# Revit family: IS_Ceralook_BC176_BIM_GB
name_source: partatom
category: Plumbing Fixtures
revit_build: Autodesk Revit 2017 (Build: 20160225_1515(x64)
units: mm (PartAtom-declared; Revit-internal decimal feet)

## family parameters
Always vertical = No
Cut with Voids When Loaded = No
OmniClass Number = 23.45.55.17
OmniClass Title = Mixing Faucets
Part Type = Normal
Room Calculation Point = No
Round Connector Dimension = Use Diameter
Shared = No
Work Plane-Based = No

## types (1)
- BC176AA - CLOOK SNK MXR SDE/HDL P/O HS/1F BLUE ST
    Accessories = www.idealspec.co.uk
    AreaUnits = millimeters
    AssetType = Fixed
    BIMObjectName = IS_IdealStandard_SinkMixer_Ceralook_BC176
    Brand = IdealStandard
    Category = Plumbing
    CisternCapacity = 0 m³
    Color = Chrome
    ConnectionType = Plumbing
    Description = BC176 CLOOK SNK MXR SDE/HDL P/O HS/1F BLUE ST
    DurationUnit = year
    ExpectedLife = 5
    Features = BC176 Sink Mixer Ceralook kitchen mixer with high spout L and handshower with BlueStart Technology
    Finish = Chrome
    FlushRate = 0 m³
    FlushingRate = 0
    HasGrabHandles = No
    HasIntegralShutOffDevice = No
    HasTray = No
    IfcExportAs = IfcValveType
    IfcExportType = FAUCETS
    InletConnectionSize = 0 mm  [stored 0 ft]
    Installation instructions = http://www.idealspec.co.uk
    InstallationInstructions = www.idealspec.co.uk/resources.html
    IsAutomaticFlush = No
    IsBuiltIn = No
    IsHighPressure = No
    IsSingleFlush = No
    LinearUnits = millimeters
    MainColor = Chrome
    ManufacturerURL = www.idealspec.co.uk
    Material = Brass
    MaterialThickness = 0 mm  [stored 0 ft]
    Model = BC176AA
    ModelNumber = BC176AA
    ModelReference = Ceralook Sink Mixer
    Name = SinkMixer_Ceralook_BC176_IdealStandard
    NettWeight = 2.211
    NominalDepth = 560 mm  [stored 1.83727 ft]
    NominalHeight = 361 mm
    NominalLength = 264 mm
    NominalWidth = 119 mm
    OutletConnectionSize = 0 mm  [stored 0 ft]
    Product group = Sink Mixer
    ProductInformation = http://www.idealspec.co.uk
    SeatHasCover = No
    Shape = Sculptured
    Size = 361 x 264 x 119mm
    SpareParts = www.fastpart-spares.co.uk
    SpilloverLevel = 0 mm  [stored 0 ft]
    TestPressure = 10 Bar
    URL = www.idealspec.co.uk
    Uniclass 2015 Code = Pr_40_20_87_84
    Uniclass 2015 Name = Sink taps
    Uniclass2015Code = Pr_40_20_87_82
    Uniclass2015Title = Sink manual water supply sets
    Uniclass2015Version = v1.1
    Version = 1
    VolumeUnits = Litres
    WarrantyDescription = Manufacturers warranty
    WarrantyDurationUnit = Year

note: [stored X ft] marks values corroborated as IEEE doubles in the binary element streams (Revit-internal decimal feet)

## geometry (parser evidence)
native form markers: Sweep x2
no freeform markers — native parametric forms only
